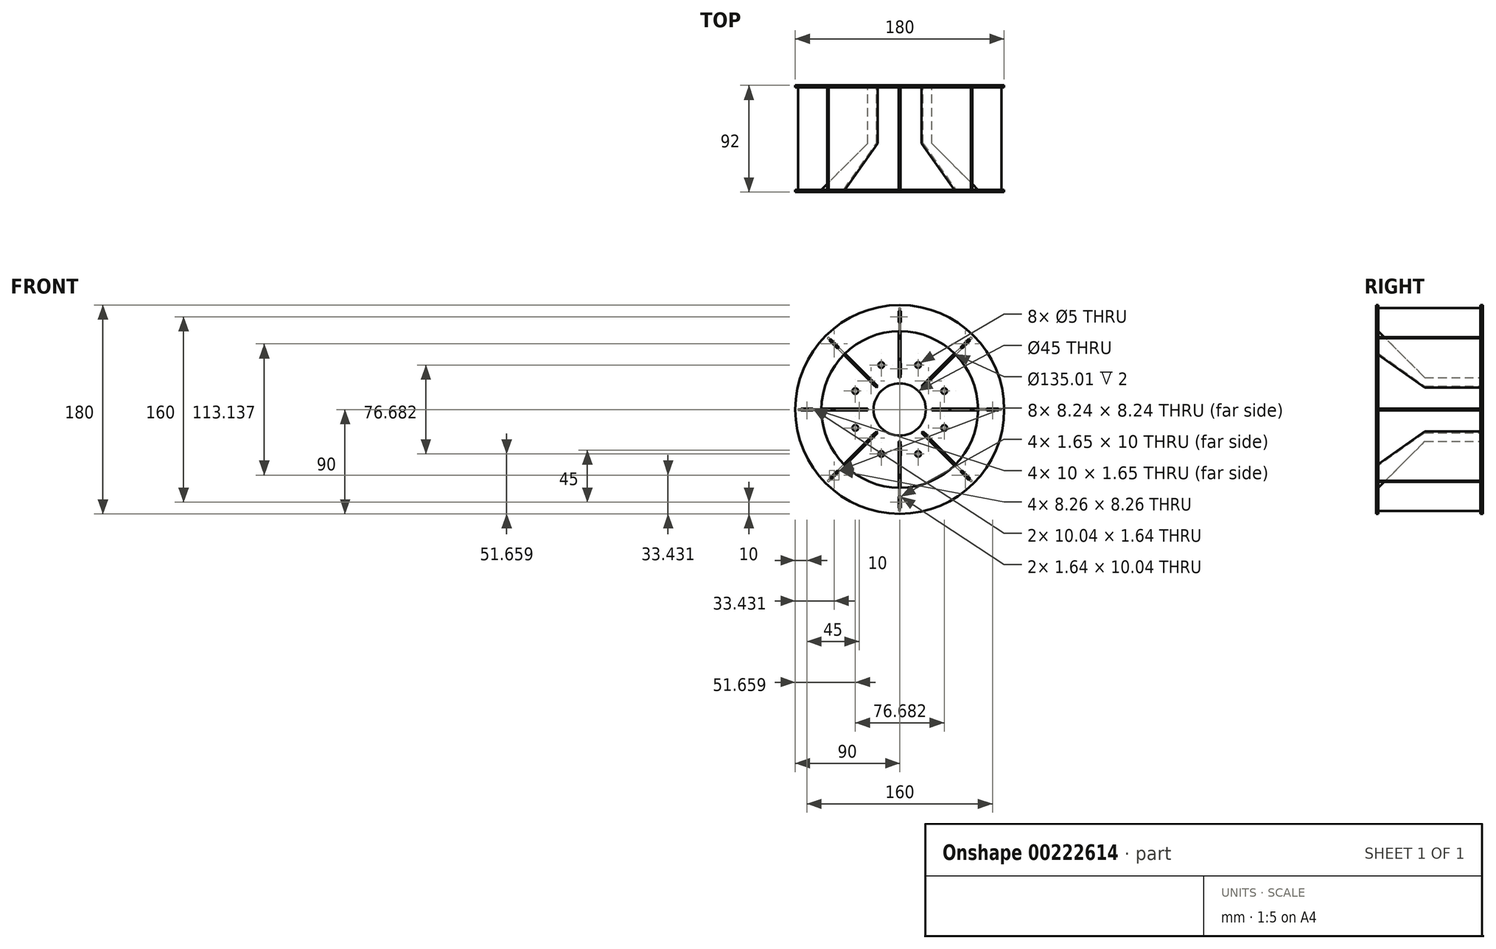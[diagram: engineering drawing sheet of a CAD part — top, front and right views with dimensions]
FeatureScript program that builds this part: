
annotation { "Feature Type Name" : "Feature", "Feature Type Description" : "" }
export const myFeature = defineFeature(function(context is Context, id is Id, definition is map)
    precondition{}
    {
        {
            var Q0;
            Q0=qCreatedBy(makeId("Front.planeOp"),FACE);
            var sketch = newSketch(context, id + "F0", { "sketchPlane" : qUnion([Q0])});
            skCircle(sketch, "E0", {"center": v(0, 0) * mm, "radius": 90 * mm});
            skCircle(sketch, "E1", {"center": v(0, 0) * mm, "radius": 22.5 * mm});
            skSolve(sketch);
        }
        {
            var Q0;
            Q0=makeQuery(id+"F0.imprint","IMPRINT",FACE,{"disambiguationData":[TD([[makeQuery(id+"F0.imprint","IMPRINT",EDGE,{"derivedFrom":sQuery(id+"F0.wireOp",EDGE,"E0")}),1.0]])]});
            var Q1;
            Q1 = qSketchRegion(id + "F2", true);
            extrude(context, id + "F1", {"entities" : qUnion([Q0, Q1]), "depth" : 2 * mm});
        }
        {
            var Q0;
            Q0=makeQuery(id+"F1.opExtrude","CAP_FACE",FACE,{"disambiguationData":[OSD([sQuery(id+"F0.wireOp",EDGE,"E0"),sQuery(id+"F0.wireOp",EDGE,"E1")])],"isStart":false});
            var sketch = newSketch(context, id + "F2", { "sketchPlane" : qUnion([Q0])});
            skLineSegment(sketch, "E2", {"start": v(0, 85) * mm, "end": v(0, 30) * mm, "construction": true});
            skLineSegment(sketch, "E3.1.0", {"start": v(-60.1, 60.1) * mm, "end": v(-21.21, 21.21) * mm});
            skLineSegment(sketch, "E3.2.0", {"start": v(-85, 0) * mm, "end": v(-30, 0) * mm});
            skLineSegment(sketch, "E3.3.0", {"start": v(-60.1, -60.1) * mm, "end": v(-21.21, -21.21) * mm});
            skLineSegment(sketch, "E3.4.0", {"start": v(0, -85) * mm, "end": v(0, -30) * mm});
            skLineSegment(sketch, "E3.5.0", {"start": v(60.1, -60.1) * mm, "end": v(21.21, -21.21) * mm});
            skLineSegment(sketch, "E3.6.0", {"start": v(85, 0) * mm, "end": v(30, 0) * mm});
            skLineSegment(sketch, "E3.7.0", {"start": v(60.1, 60.1) * mm, "end": v(21.21, 21.21) * mm});
            skPoint(sketch, "E3.center", {"position": v(0, 0) * mm});
            skPoint(sketch, "E4", {"position": v(0, 57.5) * mm});
            skSolve(sketch);
        }
        {
            var Q0;
            Q0=makeQuery(id+"F2.imprint","IMPRINT",FACE,{"disambiguationData":[TD([[makeQuery(id+"F2.imprint","IMPRINT",EDGE,{"derivedFrom":makeQuery(id+"F1.opExtrude","CAP_EDGE",EDGE,{"disambiguationData":[OSD([sQuery(id+"F0.wireOp",EDGE,"E0")])],"isStart":false})}),1.0]])]});
            var sketch = newSketch(context, id + "F3", { "sketchPlane" : qUnion([Q0])});
            skCircle(sketch, "E5", {"center": v(0, 0) * mm, "radius": 41.5 * mm, "construction": true});
            skCircle(sketch, "E6", {"center": v(15.88, 38.34) * mm, "radius": 2.5 * mm});
            skCircle(sketch, "E7.1.0", {"center": v(-15.88, 38.34) * mm, "radius": 2.5 * mm});
            skCircle(sketch, "E7.2.0", {"center": v(-38.34, 15.88) * mm, "radius": 2.5 * mm});
            skCircle(sketch, "E7.3.0", {"center": v(-38.34, -15.88) * mm, "radius": 2.5 * mm});
            skCircle(sketch, "E7.4.0", {"center": v(-15.88, -38.34) * mm, "radius": 2.5 * mm});
            skCircle(sketch, "E7.5.0", {"center": v(15.88, -38.34) * mm, "radius": 2.5 * mm});
            skCircle(sketch, "E7.6.0", {"center": v(38.34, -15.88) * mm, "radius": 2.5 * mm});
            skCircle(sketch, "E7.7.0", {"center": v(38.34, 15.88) * mm, "radius": 2.5 * mm});
            skLineSegment(sketch, "E8", {"start": v(0, 0) * mm, "end": v(30.38, 73.35) * mm, "construction": true});
            skLineSegment(sketch, "E9", {"start": v(0, 0) * mm, "end": v(0, 83.8) * mm, "construction": true});
            skSolve(sketch);
        }
        {
            var Q0;
            Q0 = qSketchRegion(id + "F3", true);
            extrude(context, id + "F4", {"entities" : qUnion([Q0]), "operationType" : NewBodyOperationType.REMOVE, "endBound" : BoundingType.THROUGH_ALL, "oppositeDirection" : true, "depth" : 25 * mm});
        }
        {
            var Q0;
            Q0=makeQuery(id+"F2.imprint","IMPRINT",FACE,{"disambiguationData":[TD([[makeQuery(id+"F2.imprint","IMPRINT",EDGE,{"derivedFrom":makeQuery(id+"F1.opExtrude","CAP_EDGE",EDGE,{"disambiguationData":[OSD([sQuery(id+"F0.wireOp",EDGE,"E0")])],"isStart":false})}),1.0]])]});
            var sketch = newSketch(context, id + "F5", { "sketchPlane" : qUnion([Q0])});
            skLineSegment(sketch, "E10", {"start": v(0.82, 85) * mm, "end": v(0.82, 75) * mm});
            skLineSegment(sketch, "E11", {"start": v(-0.82, 30) * mm, "end": v(0.82, 30) * mm});
            skLineSegment(sketch, "E12", {"start": v(-0.83, 30) * mm, "end": v(-0.83, 40) * mm});
            skLineSegment(sketch, "E13", {"start": v(-0.82, 85) * mm, "end": v(0.82, 85) * mm});
            skLineSegment(sketch, "E14", {"start": v(0.83, 75) * mm, "end": v(-0.83, 75) * mm});
            skLineSegment(sketch, "E15", {"start": v(-0.83, 40) * mm, "end": v(0.83, 40) * mm});
            skLineSegment(sketch, "E16.trimOffspring", {"start": v(-0.83, 75) * mm, "end": v(-0.83, 85) * mm});
            skLineSegment(sketch, "E17.trimOffspring", {"start": v(0.83, 40) * mm, "end": v(0.83, 30) * mm});
            skLineSegment(sketch, "E18.1.0", {"start": v(-59.52, 60.69) * mm, "end": v(-52.45, 53.62) * mm});
            skLineSegment(sketch, "E18.1.1", {"start": v(-53.62, 52.45) * mm, "end": v(-60.69, 59.52) * mm});
            skLineSegment(sketch, "E18.1.2", {"start": v(-27.7, 28.87) * mm, "end": v(-20.63, 21.8) * mm});
            skLineSegment(sketch, "E18.1.3", {"start": v(-21.8, 20.63) * mm, "end": v(-28.87, 27.7) * mm});
            skLineSegment(sketch, "E18.1.4", {"start": v(-60.69, 59.52) * mm, "end": v(-59.52, 60.69) * mm});
            skLineSegment(sketch, "E18.1.5", {"start": v(-21.8, 20.63) * mm, "end": v(-20.63, 21.8) * mm});
            skLineSegment(sketch, "E18.1.6", {"start": v(-52.45, 53.62) * mm, "end": v(-53.62, 52.45) * mm});
            skLineSegment(sketch, "E18.1.7", {"start": v(-28.87, 27.7) * mm, "end": v(-27.7, 28.87) * mm});
            skLineSegment(sketch, "E18.2.0", {"start": v(-85, 0.82) * mm, "end": v(-75, 0.83) * mm});
            skLineSegment(sketch, "E18.2.1", {"start": v(-75, -0.82) * mm, "end": v(-85, -0.82) * mm});
            skLineSegment(sketch, "E18.2.2", {"start": v(-40, 0.83) * mm, "end": v(-30, 0.83) * mm});
            skLineSegment(sketch, "E18.2.3", {"start": v(-30, -0.83) * mm, "end": v(-40, -0.82) * mm});
            skLineSegment(sketch, "E18.2.4", {"start": v(-85, -0.82) * mm, "end": v(-85, 0.82) * mm});
            skLineSegment(sketch, "E18.2.5", {"start": v(-30, -0.82) * mm, "end": v(-30, 0.83) * mm});
            skLineSegment(sketch, "E18.2.6", {"start": v(-75, 0.83) * mm, "end": v(-75, -0.82) * mm});
            skLineSegment(sketch, "E18.2.7", {"start": v(-40, -0.83) * mm, "end": v(-40, 0.83) * mm});
            skLineSegment(sketch, "E18.3.0", {"start": v(-60.69, -59.52) * mm, "end": v(-53.62, -52.45) * mm});
            skLineSegment(sketch, "E18.3.1", {"start": v(-52.45, -53.62) * mm, "end": v(-59.52, -60.69) * mm});
            skLineSegment(sketch, "E18.3.2", {"start": v(-28.87, -27.7) * mm, "end": v(-21.8, -20.63) * mm});
            skLineSegment(sketch, "E18.3.3", {"start": v(-20.63, -21.8) * mm, "end": v(-27.7, -28.87) * mm});
            skLineSegment(sketch, "E18.3.4", {"start": v(-59.52, -60.69) * mm, "end": v(-60.69, -59.52) * mm});
            skLineSegment(sketch, "E18.3.5", {"start": v(-20.63, -21.8) * mm, "end": v(-21.8, -20.63) * mm});
            skLineSegment(sketch, "E18.3.6", {"start": v(-53.62, -52.45) * mm, "end": v(-52.45, -53.62) * mm});
            skLineSegment(sketch, "E18.3.7", {"start": v(-27.7, -28.87) * mm, "end": v(-28.87, -27.7) * mm});
            skLineSegment(sketch, "E18.4.0", {"start": v(-0.83, -85) * mm, "end": v(-0.83, -75) * mm});
            skLineSegment(sketch, "E18.4.1", {"start": v(0.82, -75) * mm, "end": v(0.82, -85) * mm});
            skLineSegment(sketch, "E18.4.2", {"start": v(-0.83, -40) * mm, "end": v(-0.83, -30) * mm});
            skLineSegment(sketch, "E18.4.3", {"start": v(0.82, -30) * mm, "end": v(0.82, -40) * mm});
            skLineSegment(sketch, "E18.4.4", {"start": v(0.82, -85) * mm, "end": v(-0.82, -85) * mm});
            skLineSegment(sketch, "E18.4.5", {"start": v(0.82, -30) * mm, "end": v(-0.83, -30) * mm});
            skLineSegment(sketch, "E18.4.6", {"start": v(-0.83, -75) * mm, "end": v(0.82, -75) * mm});
            skLineSegment(sketch, "E18.4.7", {"start": v(0.83, -40) * mm, "end": v(-0.83, -40) * mm});
            skLineSegment(sketch, "E18.5.0", {"start": v(59.52, -60.69) * mm, "end": v(52.45, -53.62) * mm});
            skLineSegment(sketch, "E18.5.1", {"start": v(53.62, -52.45) * mm, "end": v(60.69, -59.52) * mm});
            skLineSegment(sketch, "E18.5.2", {"start": v(27.7, -28.87) * mm, "end": v(20.63, -21.8) * mm});
            skLineSegment(sketch, "E18.5.3", {"start": v(21.8, -20.63) * mm, "end": v(28.87, -27.7) * mm});
            skLineSegment(sketch, "E18.5.4", {"start": v(60.69, -59.52) * mm, "end": v(59.52, -60.69) * mm});
            skLineSegment(sketch, "E18.5.5", {"start": v(21.8, -20.63) * mm, "end": v(20.63, -21.8) * mm});
            skLineSegment(sketch, "E18.5.6", {"start": v(52.45, -53.62) * mm, "end": v(53.62, -52.45) * mm});
            skLineSegment(sketch, "E18.5.7", {"start": v(28.87, -27.7) * mm, "end": v(27.7, -28.87) * mm});
            skLineSegment(sketch, "E18.6.0", {"start": v(85, -0.83) * mm, "end": v(75, -0.83) * mm});
            skLineSegment(sketch, "E18.6.1", {"start": v(75, 0.82) * mm, "end": v(85, 0.82) * mm});
            skLineSegment(sketch, "E18.6.2", {"start": v(40, -0.83) * mm, "end": v(30, -0.83) * mm});
            skLineSegment(sketch, "E18.6.3", {"start": v(30, 0.82) * mm, "end": v(40, 0.82) * mm});
            skLineSegment(sketch, "E18.6.4", {"start": v(85, 0.82) * mm, "end": v(85, -0.82) * mm});
            skLineSegment(sketch, "E18.6.5", {"start": v(30, 0.82) * mm, "end": v(30, -0.83) * mm});
            skLineSegment(sketch, "E18.6.6", {"start": v(75, -0.83) * mm, "end": v(75, 0.82) * mm});
            skLineSegment(sketch, "E18.6.7", {"start": v(40, 0.83) * mm, "end": v(40, -0.83) * mm});
            skLineSegment(sketch, "E18.7.0", {"start": v(60.69, 59.52) * mm, "end": v(53.62, 52.45) * mm});
            skLineSegment(sketch, "E18.7.1", {"start": v(52.45, 53.62) * mm, "end": v(59.52, 60.69) * mm});
            skLineSegment(sketch, "E18.7.2", {"start": v(28.87, 27.7) * mm, "end": v(21.8, 20.63) * mm});
            skLineSegment(sketch, "E18.7.3", {"start": v(20.63, 21.8) * mm, "end": v(27.7, 28.87) * mm});
            skLineSegment(sketch, "E18.7.4", {"start": v(59.52, 60.69) * mm, "end": v(60.69, 59.52) * mm});
            skLineSegment(sketch, "E18.7.5", {"start": v(20.63, 21.8) * mm, "end": v(21.8, 20.63) * mm});
            skLineSegment(sketch, "E18.7.6", {"start": v(53.62, 52.45) * mm, "end": v(52.45, 53.62) * mm});
            skLineSegment(sketch, "E18.7.7", {"start": v(27.7, 28.87) * mm, "end": v(28.87, 27.7) * mm});
            skPoint(sketch, "E18.center", {"position": v(0, 0) * mm});
            skSolve(sketch);
        }
        {
            var Q0;
            Q0 = qSketchRegion(id + "F5", true);
            var Q1;
            Q1=makeQuery(id+"F1.opExtrude","SWEPT_BODY",BODY,{"disambiguationData":[OSD([sQuery(id+"F0.wireOp",EDGE,"E0"),sQuery(id+"F0.wireOp",EDGE,"E1")])]});
            extrude(context, id + "F6", {"entities" : qUnion([Q0]), "operationType" : NewBodyOperationType.REMOVE, "endBound" : BoundingType.UP_TO_BODY, "oppositeDirection" : true, "endBoundEntityBody" : qUnion([Q1]), "depth" : 25 * mm});
        }
        {
            var Q0;
            Q0=qCreatedBy(makeId("Right.planeOp"),FACE);
            var sketch = newSketch(context, id + "F7", { "sketchPlane" : qUnion([Q0])});
            skLineSegment(sketch, "E19.bottom", {"start": v(-90, 87.5) * mm, "end": v(-2, 87.5) * mm});
            skLineSegment(sketch, "E19.top", {"start": v(-90, 27.5) * mm, "end": v(-2, 27.5) * mm});
            skLineSegment(sketch, "E19.left", {"start": v(-90, 87.5) * mm, "end": v(-90, 27.5) * mm});
            skLineSegment(sketch, "E19.right", {"start": v(-2, 87.5) * mm, "end": v(-2, 27.5) * mm});
            skPoint(sketch, "E20", {"position": v(-2, 57.5) * mm});
            skPoint(sketch, "E21", {"position": v(0, 57.5) * mm});
            skLineSegment(sketch, "E22", {"start": v(-2, 57.5) * mm, "end": v(3.67, 57.5) * mm, "construction": true});
            skLineSegment(sketch, "E23", {"start": v(-90, 85) * mm, "end": v(-92, 85) * mm});
            skLineSegment(sketch, "E24", {"start": v(-92, 85) * mm, "end": v(-92, 75) * mm});
            skLineSegment(sketch, "E25", {"start": v(-92, 75) * mm, "end": v(-90, 75) * mm});
            skPoint(sketch, "E26", {"position": v(0, 79.47) * mm});
            skLineSegment(sketch, "E27.bottom", {"start": v(-2, 30.05) * mm, "end": v(0, 30.05) * mm});
            skLineSegment(sketch, "E27.top", {"start": v(-2, 39.95) * mm, "end": v(0, 39.95) * mm});
            skLineSegment(sketch, "E27.left", {"start": v(-2, 30.05) * mm, "end": v(-2, 39.95) * mm});
            skLineSegment(sketch, "E28", {"start": v(0, 39.95) * mm, "end": v(0, 30.05) * mm});
            skPoint(sketch, "E29", {"position": v(0, 35) * mm});
            skLineSegment(sketch, "E30.MirrorCS", {"start": v(-2, 84.95) * mm, "end": v(0, 84.95) * mm});
            skLineSegment(sketch, "E31.MirrorCS", {"start": v(-2, 75.05) * mm, "end": v(0, 75.05) * mm});
            skLineSegment(sketch, "E32.MirrorCS", {"start": v(0, 75.05) * mm, "end": v(0, 84.95) * mm});
            skSolve(sketch);
        }
        {
            var Q0;
            Q0 = qSketchRegion(id + "F7", true);
            extrude(context, id + "F8", {"entities" : qUnion([Q0]), "depth" : 0.8 * mm, "hasSecondDirection" : true, "secondDirectionOppositeDirection" : true, "secondDirectionDepth" : 0.8 * mm});
        }
        {
            var Q0;
            Q0=makeQuery(id+"F8.opExtrude","SWEPT_EDGE",EDGE,{"disambiguationData":[OSD([sQuery(id+"F7.wireOp",EDGE,"E19.top"),sQuery(id+"F7.wireOp",EDGE,"E19.left")])]});
            chamfer(context, id + "F9", {"entities" : qUnion([Q0]), "width" : 40 * mm, "tangentPropagation" : true});
        }
        {
            var Q0;
            Q0=qCreatedBy(makeId("Right.planeOp"),FACE);
            var sketch = newSketch(context, id + "F10", { "sketchPlane" : qUnion([Q0])});
            skLineSegment(sketch, "E33", {"start": v(0, 0) * mm, "end": v(-127.4, 0) * mm, "construction": true});
            skSolve(sketch);
        }
        {
            var Q0;
            Q0=makeQuery(id+"F8.opExtrude","SWEPT_BODY",BODY,{"disambiguationData":[OSD([sQuery(id+"F7.wireOp",EDGE,"E19.bottom"),sQuery(id+"F7.wireOp",EDGE,"E19.top"),sQuery(id+"F7.wireOp",EDGE,"E19.left"),sQuery(id+"F7.wireOp",EDGE,"E19.right"),sQuery(id+"F7.wireOp",EDGE,"5v18hPcZ-jpDL-uz0S-qqKi-jI18Y4yTBnZ8"),sQuery(id+"F7.wireOp",EDGE,"HFg0nzKB-dCV6-C93R-9se7-hoVBX2ey2Nsq"),sQuery(id+"F7.wireOp",EDGE,"EIBWVb18-DvKT-R63i-Z0Nx-Z1OrTEkgvxSv"),sQuery(id+"F7.wireOp",EDGE,"E23"),sQuery(id+"F7.wireOp",EDGE,"E24"),sQuery(id+"F7.wireOp",EDGE,"E25")])]});
            var Q1;
            Q1=sQuery(id+"F10.wireOp",EDGE,"E33");
            circularPattern(context, id + "F11", {"entities" : qUnion([Q0]), "axis" : qUnion([Q1]), "angle" : 360 * degree, "instanceCount" : 8, "equalSpace" : true});
        }
        {
            var Q0;
            {var subQ0=sQuery(id+"F7.wireOp",EDGE,"E19.left");Q0=makeQuery(id+"F11.opPattern","COPY",FACE,{"derivedFrom":makeQuery(id+"F8.opExtrude","SWEPT_FACE",FACE,{"disambiguationData":[OSD([subQ0]),TDD([makeQuery(id+"F7.imprint","IMPRINT",EDGE,{"disambiguationData":[TD([[makeQuery(id+"F7.imprint","INTERSECT",VERTEX,{"derivedFrom":[sQuery(id+"F7.wireOp",EDGE,"E19.top"),subQ0]}),1.0]])],"derivedFrom":subQ0})])]}),"instanceName":"6"});}
            var sketch = newSketch(context, id + "F12", { "sketchPlane" : qUnion([Q0])});
            skCircle(sketch, "E34", {"center": v(0, 0) * mm, "radius": 90 * mm});
            skCircle(sketch, "E35", {"center": v(0, 0) * mm, "radius": 67.5 * mm});
            skLineSegment(sketch, "E36.0.0", {"start": v(-0.8, 85) * mm, "end": v(-0.8, 75) * mm, "construction": true});
            skLineSegment(sketch, "E36.0.1", {"start": v(-0.8, 75) * mm, "end": v(0.8, 75) * mm, "construction": true});
            skLineSegment(sketch, "E36.0.2", {"start": v(0.8, 75) * mm, "end": v(0.8, 85) * mm, "construction": true});
            skLineSegment(sketch, "E36.0.3", {"start": v(0.8, 85) * mm, "end": v(-0.8, 85) * mm, "construction": true});
            skLineSegment(sketch, "E37.0", {"start": v(0.82, 74.98) * mm, "end": v(0.82, 85.02) * mm});
            skLineSegment(sketch, "E37.1", {"start": v(-0.82, 74.98) * mm, "end": v(0.82, 74.98) * mm});
            skLineSegment(sketch, "E37.2", {"start": v(-0.82, 85.02) * mm, "end": v(-0.82, 74.98) * mm});
            skLineSegment(sketch, "E37.3", {"start": v(0.82, 85.02) * mm, "end": v(-0.82, 85.02) * mm});
            skLineSegment(sketch, "E38.1.0", {"start": v(-52.44, 53.6) * mm, "end": v(-59.54, 60.7) * mm});
            skLineSegment(sketch, "E38.1.1", {"start": v(-52.47, 53.6) * mm, "end": v(-59.54, 60.67) * mm, "construction": true});
            skLineSegment(sketch, "E38.1.2", {"start": v(-60.67, 59.54) * mm, "end": v(-53.6, 52.47) * mm, "construction": true});
            skLineSegment(sketch, "E38.1.3", {"start": v(-60.7, 59.54) * mm, "end": v(-53.6, 52.44) * mm});
            skLineSegment(sketch, "E38.1.4", {"start": v(-59.54, 60.67) * mm, "end": v(-60.67, 59.54) * mm, "construction": true});
            skLineSegment(sketch, "E38.1.5", {"start": v(-53.6, 52.47) * mm, "end": v(-52.47, 53.6) * mm, "construction": true});
            skLineSegment(sketch, "E38.1.6", {"start": v(-59.54, 60.7) * mm, "end": v(-60.7, 59.54) * mm});
            skLineSegment(sketch, "E38.1.7", {"start": v(-53.6, 52.44) * mm, "end": v(-52.44, 53.6) * mm});
            skLineSegment(sketch, "E38.2.0", {"start": v(-74.98, 0.82) * mm, "end": v(-85.02, 0.82) * mm});
            skLineSegment(sketch, "E38.2.1", {"start": v(-75, 0.8) * mm, "end": v(-85, 0.8) * mm, "construction": true});
            skLineSegment(sketch, "E38.2.2", {"start": v(-85, -0.8) * mm, "end": v(-75, -0.8) * mm, "construction": true});
            skLineSegment(sketch, "E38.2.3", {"start": v(-85.02, -0.82) * mm, "end": v(-74.98, -0.82) * mm});
            skLineSegment(sketch, "E38.2.4", {"start": v(-85, 0.8) * mm, "end": v(-85, -0.8) * mm, "construction": true});
            skLineSegment(sketch, "E38.2.5", {"start": v(-75, -0.8) * mm, "end": v(-75, 0.8) * mm, "construction": true});
            skLineSegment(sketch, "E38.2.6", {"start": v(-85.02, 0.82) * mm, "end": v(-85.02, -0.82) * mm});
            skLineSegment(sketch, "E38.2.7", {"start": v(-74.98, -0.82) * mm, "end": v(-74.98, 0.82) * mm});
            skLineSegment(sketch, "E38.3.0", {"start": v(-53.6, -52.44) * mm, "end": v(-60.7, -59.54) * mm});
            skLineSegment(sketch, "E38.3.1", {"start": v(-53.6, -52.47) * mm, "end": v(-60.67, -59.54) * mm, "construction": true});
            skLineSegment(sketch, "E38.3.2", {"start": v(-59.54, -60.67) * mm, "end": v(-52.47, -53.6) * mm, "construction": true});
            skLineSegment(sketch, "E38.3.3", {"start": v(-59.54, -60.7) * mm, "end": v(-52.44, -53.6) * mm});
            skLineSegment(sketch, "E38.3.4", {"start": v(-60.67, -59.54) * mm, "end": v(-59.54, -60.67) * mm, "construction": true});
            skLineSegment(sketch, "E38.3.5", {"start": v(-52.47, -53.6) * mm, "end": v(-53.6, -52.47) * mm, "construction": true});
            skLineSegment(sketch, "E38.3.6", {"start": v(-60.7, -59.54) * mm, "end": v(-59.54, -60.7) * mm});
            skLineSegment(sketch, "E38.3.7", {"start": v(-52.44, -53.6) * mm, "end": v(-53.6, -52.44) * mm});
            skLineSegment(sketch, "E38.4.0", {"start": v(-0.82, -74.98) * mm, "end": v(-0.82, -85.02) * mm});
            skLineSegment(sketch, "E38.4.1", {"start": v(-0.8, -75) * mm, "end": v(-0.8, -85) * mm, "construction": true});
            skLineSegment(sketch, "E38.4.2", {"start": v(0.8, -85) * mm, "end": v(0.8, -75) * mm, "construction": true});
            skLineSegment(sketch, "E38.4.3", {"start": v(0.82, -85.02) * mm, "end": v(0.82, -74.98) * mm});
            skLineSegment(sketch, "E38.4.4", {"start": v(-0.8, -85) * mm, "end": v(0.8, -85) * mm, "construction": true});
            skLineSegment(sketch, "E38.4.5", {"start": v(0.8, -75) * mm, "end": v(-0.8, -75) * mm, "construction": true});
            skLineSegment(sketch, "E38.4.6", {"start": v(-0.82, -85.02) * mm, "end": v(0.82, -85.02) * mm});
            skLineSegment(sketch, "E38.4.7", {"start": v(0.82, -74.98) * mm, "end": v(-0.82, -74.98) * mm});
            skLineSegment(sketch, "E38.5.0", {"start": v(52.44, -53.6) * mm, "end": v(59.54, -60.7) * mm});
            skLineSegment(sketch, "E38.5.1", {"start": v(52.47, -53.6) * mm, "end": v(59.54, -60.67) * mm, "construction": true});
            skLineSegment(sketch, "E38.5.2", {"start": v(60.67, -59.54) * mm, "end": v(53.6, -52.47) * mm, "construction": true});
            skLineSegment(sketch, "E38.5.3", {"start": v(60.7, -59.54) * mm, "end": v(53.6, -52.44) * mm});
            skLineSegment(sketch, "E38.5.4", {"start": v(59.54, -60.67) * mm, "end": v(60.67, -59.54) * mm, "construction": true});
            skLineSegment(sketch, "E38.5.5", {"start": v(53.6, -52.47) * mm, "end": v(52.47, -53.6) * mm, "construction": true});
            skLineSegment(sketch, "E38.5.6", {"start": v(59.54, -60.7) * mm, "end": v(60.7, -59.54) * mm});
            skLineSegment(sketch, "E38.5.7", {"start": v(53.6, -52.44) * mm, "end": v(52.44, -53.6) * mm});
            skLineSegment(sketch, "E38.6.0", {"start": v(74.98, -0.82) * mm, "end": v(85.02, -0.82) * mm});
            skLineSegment(sketch, "E38.6.1", {"start": v(75, -0.8) * mm, "end": v(85, -0.8) * mm, "construction": true});
            skLineSegment(sketch, "E38.6.2", {"start": v(85, 0.8) * mm, "end": v(75, 0.8) * mm, "construction": true});
            skLineSegment(sketch, "E38.6.3", {"start": v(85.02, 0.82) * mm, "end": v(74.98, 0.82) * mm});
            skLineSegment(sketch, "E38.6.4", {"start": v(85, -0.8) * mm, "end": v(85, 0.8) * mm, "construction": true});
            skLineSegment(sketch, "E38.6.5", {"start": v(75, 0.8) * mm, "end": v(75, -0.8) * mm, "construction": true});
            skLineSegment(sketch, "E38.6.6", {"start": v(85.02, -0.82) * mm, "end": v(85.02, 0.82) * mm});
            skLineSegment(sketch, "E38.6.7", {"start": v(74.98, 0.82) * mm, "end": v(74.98, -0.82) * mm});
            skLineSegment(sketch, "E38.7.0", {"start": v(53.6, 52.44) * mm, "end": v(60.7, 59.54) * mm});
            skLineSegment(sketch, "E38.7.1", {"start": v(53.6, 52.47) * mm, "end": v(60.67, 59.54) * mm, "construction": true});
            skLineSegment(sketch, "E38.7.2", {"start": v(59.54, 60.67) * mm, "end": v(52.47, 53.6) * mm, "construction": true});
            skLineSegment(sketch, "E38.7.3", {"start": v(59.54, 60.7) * mm, "end": v(52.44, 53.6) * mm});
            skLineSegment(sketch, "E38.7.4", {"start": v(60.67, 59.54) * mm, "end": v(59.54, 60.67) * mm, "construction": true});
            skLineSegment(sketch, "E38.7.5", {"start": v(52.47, 53.6) * mm, "end": v(53.6, 52.47) * mm, "construction": true});
            skLineSegment(sketch, "E38.7.6", {"start": v(60.7, 59.54) * mm, "end": v(59.54, 60.7) * mm});
            skLineSegment(sketch, "E38.7.7", {"start": v(52.44, 53.6) * mm, "end": v(53.6, 52.44) * mm});
            skSolve(sketch);
        }
        {
            var Q0;
            Q0 = qSketchRegion(id + "F12", true);
            extrude(context, id + "F13", {"entities" : qUnion([Q0]), "depth" : 2 * mm});
        }
    });
